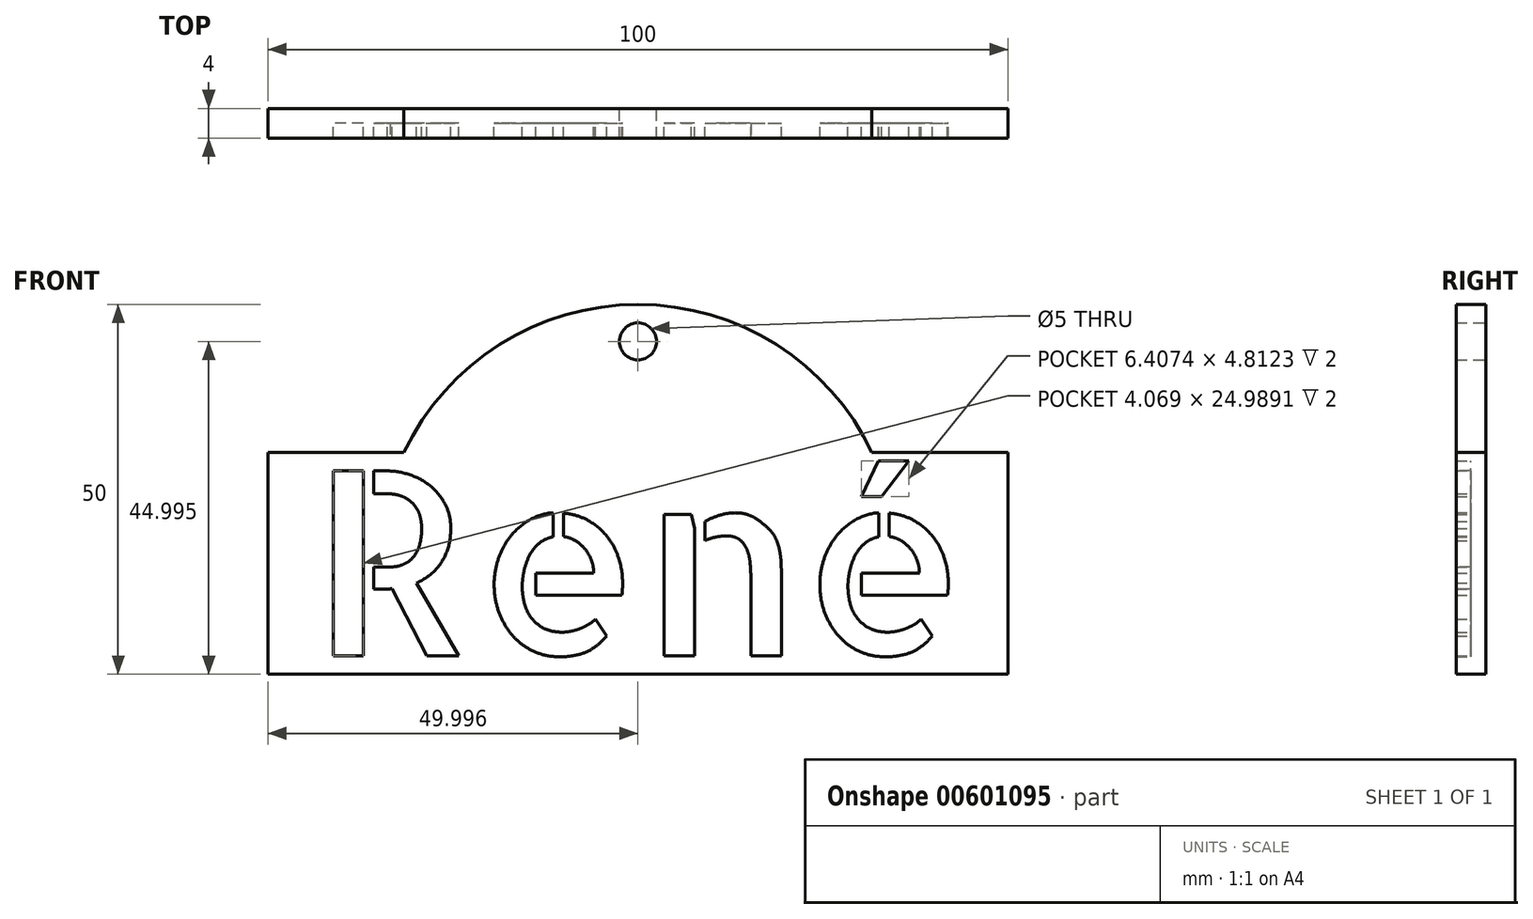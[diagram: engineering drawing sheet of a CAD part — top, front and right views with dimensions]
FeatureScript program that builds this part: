
annotation { "Feature Type Name" : "Feature", "Feature Type Description" : "" }
export const myFeature = defineFeature(function(context is Context, id is Id, definition is map)
    precondition{}
    {
        {
            var Q0;
            Q0=qCreatedBy(makeId("Front.planeOp"),FACE);
            var sketch = newSketch(context, id + "F0", { "sketchPlane" : qUnion([Q0])});
            skLineSegment(sketch, "E0.bottom", {"start": v(-17.41, 14.96) * mm, "end": v(-117.41, 14.96) * mm});
            skLineSegment(sketch, "E0.top", {"start": v(-17.41, 44.96) * mm, "end": v(-35.8, 44.96) * mm});
            skLineSegment(sketch, "E0.left", {"start": v(-17.41, 14.96) * mm, "end": v(-17.41, 44.96) * mm});
            skLineSegment(sketch, "E0.right", {"start": v(-117.41, 14.96) * mm, "end": v(-117.41, 44.96) * mm});
            skPoint(sketch, "E0.middle", {"position": v(-67.41, 29.96) * mm});
            skArc(sketch, "E1", {"start": v(-35.8, 44.96) * mm, "mid": v(-67.41, 64.96) * mm, "end": v(-99.04, 44.96) * mm});
            skPoint(sketch, "E2", {"position": v(-67.41, 14.96) * mm});
            skPoint(sketch, "E3", {"position": v(-117.41, 29.96) * mm});
            skCircle(sketch, "E4", {"center": v(-67.41, 59.96) * mm, "radius": 2.5 * mm});
            skText(sketch, "E5", { "text": "René\n", "fontName": "AllertaStencil-Regular.ttf"});
            skPoint(sketch, "E6", {"position": v(-23.15, 29.96) * mm});
            skPoint(sketch, "E7", {"position": v(-67.41, 17.46) * mm});
            skLineSegment(sketch, "E8.trimOffspring", {"start": v(-99.04, 44.96) * mm, "end": v(-117.41, 44.96) * mm});
            const initialGuessF0  = {"E5": [-0.11167, 0.01746, 1, 0, 0.025]};
            skSetInitialGuess(sketch, initialGuessF0);
            skSolve(sketch);
        }
        {
            var Q0;
            Q0 = qSketchRegion(id + "F0", true);
            var Q1;
            Q1=makeQuery(id+"F0.imprint","IMPRINT",FACE,{"disambiguationData":[TD([[makeQuery(id+"F0.imprint","IMPRINT",EDGE,{"derivedFrom":sQuery(id+"F0.wireOp",EDGE,"E0.bottom")}),-1.0]])]});
            var Q2;
            Q2=makeQuery(id+"F0.imprint","IMPRINT",FACE,{"disambiguationData":[TD([[makeQuery(id+"F0.imprint","IMPRINT",EDGE,{"derivedFrom":sQuery(id+"F0.wireOp",EDGE,"E5.sketch_text.stroke-128")}),-1.0]])]});
            var Q3;
            Q3=makeQuery(id+"F0.imprint","IMPRINT",FACE,{"disambiguationData":[TD([[makeQuery(id+"F0.imprint","IMPRINT",EDGE,{"derivedFrom":sQuery(id+"F0.wireOp",EDGE,"E5.sketch_text.stroke-104")}),-1.0]])]});
            var Q4;
            Q4=makeQuery(id+"F0.imprint","IMPRINT",FACE,{"disambiguationData":[TD([[makeQuery(id+"F0.imprint","IMPRINT",EDGE,{"derivedFrom":sQuery(id+"F0.wireOp",EDGE,"E5.sketch_text.stroke-91")}),-1.0]])]});
            var Q5;
            Q5=makeQuery(id+"F0.imprint","IMPRINT",FACE,{"disambiguationData":[TD([[makeQuery(id+"F0.imprint","IMPRINT",EDGE,{"derivedFrom":sQuery(id+"F0.wireOp",EDGE,"E5.sketch_text.stroke-72")}),-1.0]])]});
            var Q6;
            Q6=makeQuery(id+"F0.imprint","IMPRINT",FACE,{"disambiguationData":[TD([[makeQuery(id+"F0.imprint","IMPRINT",EDGE,{"derivedFrom":sQuery(id+"F0.wireOp",EDGE,"E5.sketch_text.stroke-67")}),-1.0]])]});
            var Q7;
            Q7=makeQuery(id+"F0.imprint","IMPRINT",FACE,{"disambiguationData":[TD([[makeQuery(id+"F0.imprint","IMPRINT",EDGE,{"derivedFrom":sQuery(id+"F0.wireOp",EDGE,"E5.sketch_text.stroke-43")}),-1.0]])]});
            var Q8;
            Q8=makeQuery(id+"F0.imprint","IMPRINT",FACE,{"disambiguationData":[TD([[makeQuery(id+"F0.imprint","IMPRINT",EDGE,{"derivedFrom":sQuery(id+"F0.wireOp",EDGE,"E5.sketch_text.stroke-30")}),-1.0]])]});
            var Q9;
            Q9=makeQuery(id+"F0.imprint","IMPRINT",FACE,{"disambiguationData":[TD([[makeQuery(id+"F0.imprint","IMPRINT",EDGE,{"derivedFrom":sQuery(id+"F0.wireOp",EDGE,"E5.sketch_text.stroke-4")}),-1.0]])]});
            var Q10;
            Q10=makeQuery(id+"F0.imprint","IMPRINT",FACE,{"disambiguationData":[TD([[makeQuery(id+"F0.imprint","IMPRINT",EDGE,{"derivedFrom":sQuery(id+"F0.wireOp",EDGE,"E5.sketch_text.stroke-0")}),-1.0]])]});
            extrude(context, id + "F1", {"entities" : qUnion([Q0, Q1, Q2, Q3, Q4, Q5, Q6, Q7, Q8, Q9, Q10]), "depth" : 2 * mm, "offsetDistance" : 25 * mm});
        }
        {
            var Q0;
            Q0=makeQuery(id+"F0.imprint","IMPRINT",FACE,{"disambiguationData":[TD([[makeQuery(id+"F0.imprint","IMPRINT",EDGE,{"derivedFrom":sQuery(id+"F0.wireOp",EDGE,"E0.bottom")}),-1.0]])]});
            extrude(context, id + "F2", {"entities" : qUnion([Q0]), "operationType" : NewBodyOperationType.ADD, "depth" : 4 * mm, "offsetDistance" : 25 * mm});
        }
    });
